# Revit family: LAC-LS
name_source: partatom
category: Lighting Fixtures
revit_build: Autodesk Revit 2014 (Build: 20130709_2115(x64)
units: mm (PartAtom-declared; Revit-internal decimal feet)

## types (1)
- 12"W x 4"D x 14"H
    Back Plate = Aluminium
    Color Filter = 16777215
    Comments = This model is for use in spatial massing and rendering. Please contact LightArt for pick-point placement and installation details.
    Diffuser = White Opal Acrylic
    Dimming Compatibility = Dimming Option Available
    Dimming Lamp Color Temperature Shift = <None>
    Driver = 24v
    Emit from Line Length = 0' - 5 1/2"
    HARDWARE = White powdercoated backplate mounts
to standard junction box in wall
(provided by others)
    Hardware = Silver
    LIGHTING = 1) 18W GU24 Base CFL
3500K 82 CRI light source
120V standard; 277V option available
LED option available
Dimming option available
UL Labeled
    Light Source Symbol Size = 0' - 6"
    Manufacturer = LightArt
    Model = LAC-LS
    STANDARDS = Customizable dimensions, materials,
hardware and lighting
4-6 week lead time
10,000+ 3form material options
1 year limited warranty
Pricing based on maximum sheet yield and
PGB material
Contact for custom pricing

## geometry (parser evidence)
native form markers: Sweep x8
no freeform markers — native parametric forms only
